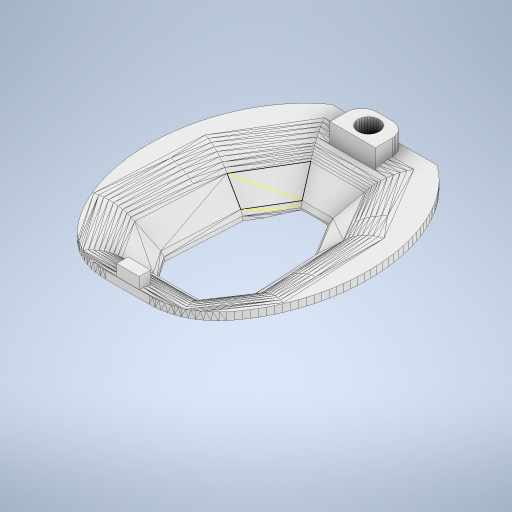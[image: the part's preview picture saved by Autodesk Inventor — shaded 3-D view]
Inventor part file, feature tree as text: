
AUTODESK INVENTOR PART (.ipt)
format: ipt  version: 2023.5 (Build 275446000, 446)  size: 1,025,536 bytes
history: native  units: in
note: dims shown in document units (in); Inventor stores cm internally (conversion verified against a paired STEP export)
features: other x2, sketch x1
ambient origin geometry x8: Origin, YZ Plane, XZ Plane, XY Plane, X Axis, Y Axis, Z Axis, Center Point
bodies: Solid1 (feature_tree)
feature tree (3):
  other  "rat_cap_base_v8"
  other  "MeshFeature1"
  sketch  "Sketch1"
